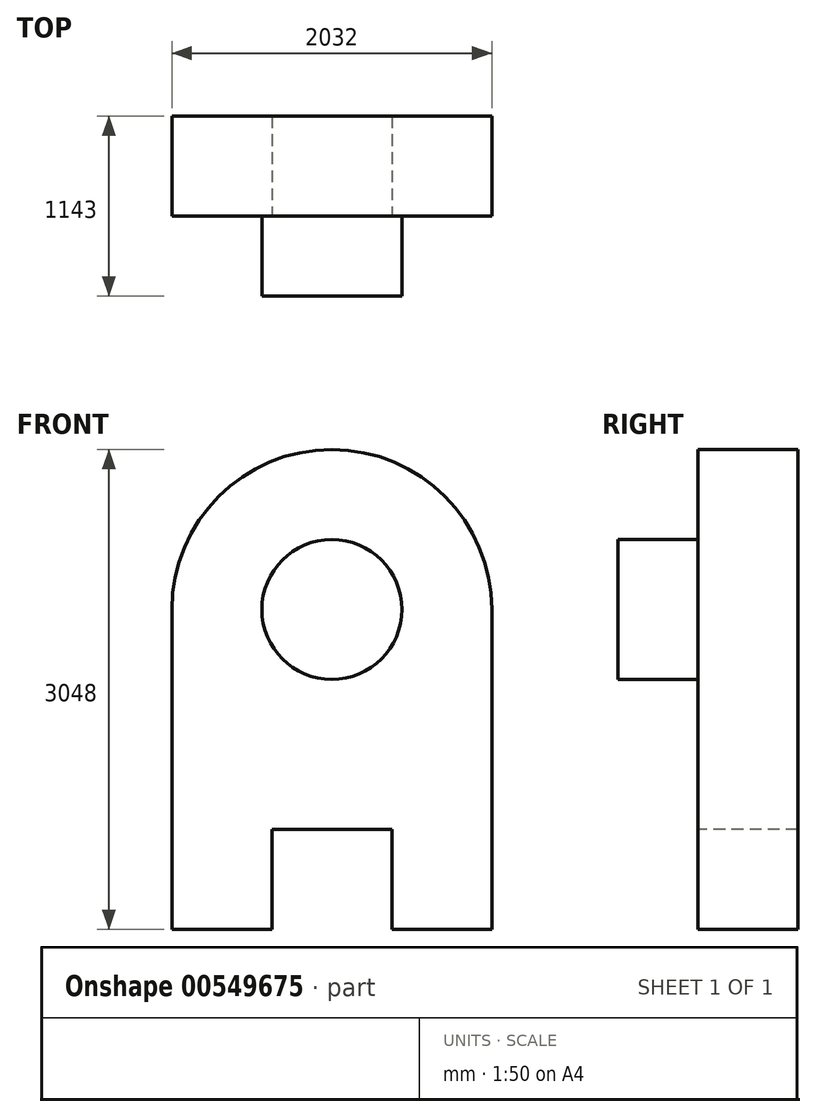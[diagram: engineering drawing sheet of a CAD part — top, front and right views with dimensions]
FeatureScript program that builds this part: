
annotation { "Feature Type Name" : "Feature", "Feature Type Description" : "" }
export const myFeature = defineFeature(function(context is Context, id is Id, definition is map)
    precondition{}
    {
        {
            var Q0;
            Q0=qCreatedBy(makeId("Front.planeOp"),FACE);
            var sketch = newSketch(context, id + "F0", { "sketchPlane" : qUnion([Q0])});
            skLineSegment(sketch, "E0.bottom", {"start": v(1016, -1016) * mm, "end": v(-1016, -1016) * mm});
            skLineSegment(sketch, "E0.top", {"start": v(1016, 1016) * mm, "end": v(-1016, 1016) * mm});
            skLineSegment(sketch, "E0.left", {"start": v(1016, -1016) * mm, "end": v(1016, 1016) * mm});
            skLineSegment(sketch, "E0.right", {"start": v(-1016, -1016) * mm, "end": v(-1016, 1016) * mm});
            skPoint(sketch, "E0.middle", {"position": v(0, 0) * mm});
            skSolve(sketch);
        }
        {
            var Q0;
            Q0 = qSketchRegion(id + "F0", true);
            extrude(context, id + "F1", {"entities" : qUnion([Q0]), "depth" : 635 * mm, "offsetDistance" : 25.4 * mm});
        }
        {
            var Q0;
            Q0=makeQuery(id+"F1.opExtrude","CAP_FACE",FACE,{"disambiguationData":[OSD([sQuery(id+"F0.wireOp",EDGE,"E0.bottom"),sQuery(id+"F0.wireOp",EDGE,"E0.top"),sQuery(id+"F0.wireOp",EDGE,"E0.left"),sQuery(id+"F0.wireOp",EDGE,"E0.right")])],"isStart":false});
            var sketch = newSketch(context, id + "F2", { "sketchPlane" : qUnion([Q0])});
            skLineSegment(sketch, "E1.bottom", {"start": v(381, -1651) * mm, "end": v(-381, -1651) * mm});
            skLineSegment(sketch, "E1.top", {"start": v(381, -381) * mm, "end": v(-381, -381) * mm});
            skLineSegment(sketch, "E1.left", {"start": v(381, -1651) * mm, "end": v(381, -381) * mm});
            skLineSegment(sketch, "E1.right", {"start": v(-381, -1651) * mm, "end": v(-381, -381) * mm});
            skPoint(sketch, "E1.middle", {"position": v(0, -1016) * mm});
            skSolve(sketch);
        }
        {
            var Q0;
            {var subQ0=sQuery(id+"F2.wireOp",EDGE,"E1.top");Q0=makeQuery(id+"F2.imprint","IMPRINT",FACE,{"disambiguationData":[TD([[makeQuery(id+"F2.imprint","IMPRINT",EDGE,{"derivedFrom":subQ0}),1.0]])]});}
            extrude(context, id + "F3", {"entities" : qUnion([Q0]), "operationType" : NewBodyOperationType.REMOVE, "endBound" : BoundingType.THROUGH_ALL, "oppositeDirection" : true, "depth" : 25.4 * mm, "offsetDistance" : 25.4 * mm});
        }
        {
            var Q0;
            Q0=makeQuery(id+"F1.opExtrude","CAP_FACE",FACE,{"disambiguationData":[OSD([sQuery(id+"F0.wireOp",EDGE,"E0.bottom"),sQuery(id+"F0.wireOp",EDGE,"E0.top"),sQuery(id+"F0.wireOp",EDGE,"E0.left"),sQuery(id+"F0.wireOp",EDGE,"E0.right")])],"isStart":false});
            var sketch = newSketch(context, id + "F4", { "sketchPlane" : qUnion([Q0])});
            skArc(sketch, "E2", {"start": v(1016, 1016) * mm, "mid": v(0, 2032) * mm, "end": v(-1016, 1016) * mm});
            skSolve(sketch);
        }
        {
            var Q0;
            Q0 = qSketchRegion(id + "F4", true);
            var Q1;
            Q1=makeQuery(id+"F4.imprint","IMPRINT",FACE,{"disambiguationData":[TD([[makeQuery(id+"F4.imprint","IMPRINT",EDGE,{"derivedFrom":sQuery(id+"F4.wireOp",EDGE,"E2")}),1.0]])]});
            extrude(context, id + "F5", {"entities" : qUnion([Q0, Q1]), "operationType" : NewBodyOperationType.ADD, "oppositeDirection" : true, "depth" : 635 * mm, "offsetDistance" : 25.4 * mm});
        }
        {
            var Q0;
            {var subQ0=sQuery(id+"F0.wireOp",EDGE,"E0.top");Q0=makeQuery(id+"F5.boolean.opBoolean","MERGE",FACE,{"derivedFrom":[makeQuery(id+"F1.opExtrude","CAP_FACE",FACE,{"disambiguationData":[OSD([sQuery(id+"F0.wireOp",EDGE,"E0.bottom"),subQ0,sQuery(id+"F0.wireOp",EDGE,"E0.left"),sQuery(id+"F0.wireOp",EDGE,"E0.right")])],"isStart":false}),makeQuery(id+"F5.opExtrude","CAP_FACE",FACE,{"disambiguationData":[OSD([subQ0,sQuery(id+"F4.wireOp",EDGE,"E2")])],"isStart":true})]});}
            var sketch = newSketch(context, id + "F6", { "sketchPlane" : qUnion([Q0])});
            skCircle(sketch, "E3", {"center": v(0, 1016) * mm, "radius": 444.5 * mm});
            skPoint(sketch, "E3.centerSnap0", {"position": v(0, 2032) * mm});
            skSolve(sketch);
        }
        {
            var Q0;
            Q0=makeQuery(id+"F6.imprint","IMPRINT",FACE,{"disambiguationData":[TD([[makeQuery(id+"F6.imprint","IMPRINT",EDGE,{"derivedFrom":sQuery(id+"F6.wireOp",EDGE,"E3")}),1.0]])]});
            extrude(context, id + "F7", {"entities" : qUnion([Q0]), "operationType" : NewBodyOperationType.ADD, "depth" : 508 * mm, "offsetDistance" : 25.4 * mm});
        }
    });
